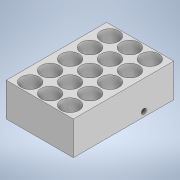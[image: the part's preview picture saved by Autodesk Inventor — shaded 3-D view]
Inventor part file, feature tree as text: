
AUTODESK INVENTOR PART (.ipt)
format: ipt  version: 2020 (Build 240168000, 168)  size: 199,168 bytes
history: native  units: in
note: dims shown in document units (in); Inventor stores cm internally (conversion verified against a paired STEP export)
features: sketch x6, hole x5, extrude x1, pattern_linear x1
ambient origin geometry x8: Origin, YZ Plane, XZ Plane, XY Plane, X Axis, Y Axis, Z Axis, Center Point
bodies: Solid1 (feature_tree)
feature tree (13):
  extrude  "Extrusion1"  Depth=5.0299in
  hole  "Hole1"  [1 undecoded]
  hole  "Hole2"  [1 undecoded]
  pattern_linear  "Rectangular Pattern1"  Spacing1=1.6811in  [1 undecoded]
  hole  "Hole3"  [1 undecoded]
  hole  "Hole4"  [1 undecoded]
  hole  "Hole5"  [1 undecoded]
  sketch  "Sketch1"  dims[d0=3.3654in d1=5.0299in]
  sketch  "Sketch2"  dims[d2=1.0in d3=135.0deg]
  sketch  "Sketch4"  dims[d4=1.0in d5=1.0in]
  sketch  "Sketch5"  dims[d6=135.0deg]
  sketch  "Sketch6"  dims[d7=1.0in]
  sketch  "Sketch7"  dims[d8=45.0deg d9=1.6811in d10=0.0in d11=1.0in d12=135.0deg d13=1.0in d14=135.0deg d15=1.0in d16=45.0deg d17=1.0in d18=45.0deg d19=0.145in d20=0.25in d21=0.375in d22=0.19in d23=0.5635in d24=0.375in d25=0.8108in d28=0.9055in d29=0.25in d30=0.375in d31=0.25in d32=0.5635in d33=1.1811in d34=0.0in d35=1.1811in d37=1.0in d38=1.9685in d40=1.0in d41=0.6825in d42=0.5165in d43=1.5in d44=0.25in d45=0.25in d46=0.25in d47=0.119in d48=0.25in d49=0.5635in d50=1.25in d51=0.8108in d52=0.25in d53=0.125in d54=0.25in d55=0.119in d56=0.25in d57=0.5635in d58=2.0in d59=0.8108in d60=1.5in d61=0.25in d62=0.25in d63=0.25in d64=0.119in d65=0.25in d66=0.5635in d67=1.25in d68=0.8108in]
note: 6 required parameter values undecoded (feature->parameter linkage not recoverable at this tier; creation-order binding heuristic only, values carry confidence <= 0.55)
